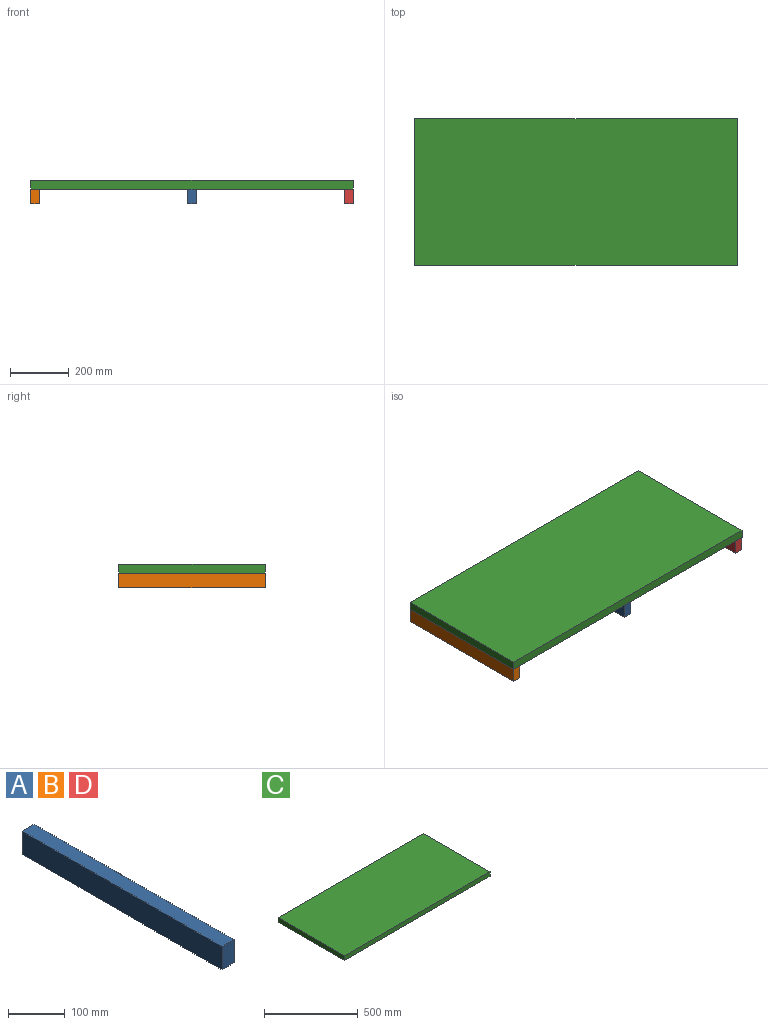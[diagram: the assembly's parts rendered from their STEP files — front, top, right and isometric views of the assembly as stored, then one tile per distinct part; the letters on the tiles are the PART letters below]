
ASSEMBLY  parts=4 mates=9
PART A: 6 faces, bbox 30x500x50 mm
  f0: plane 50x30mm, normal (0,-1,0), area 1500mm2, adj f1,f3,f4,f5
  f1: plane 500x30mm, normal (0,0,1), area 15000mm2, adj f0,f2,f4,f5
  f2: plane 50x30mm, normal (0,1,0), area 1500mm2, adj f1,f3,f4,f5
  f3: plane 500x30mm, normal (0,0,-1), area 15000mm2, adj f0,f2,f4,f5
  f4: plane 500x50mm, normal (1,0,0), area 25000mm2, adj f0,f1,f2,f3
  f5: plane 500x50mm, normal (-1,0,0), area 25000mm2, adj f0,f1,f2,f3
PART B: same geometry as A
PART C: 6 faces, bbox 1100x500x30 mm
  f0: plane 1100x30mm, normal (0,1,0), area 33000mm2, adj f1,f3,f4,f5
  f1: plane 500x30mm, normal (-1,0,0), area 15000mm2, adj f0,f2,f4,f5
  f2: plane 1100x30mm, normal (0,-1,0), area 33000mm2, adj f1,f3,f4,f5
  f3: plane 500x30mm, normal (1,0,0), area 15000mm2, adj f0,f2,f4,f5
  f4: plane 1100x500mm, normal (0,0,-1), area 550000mm2, adj f0,f1,f2,f3
  f5: plane 1100x500mm, normal (0,0,1), area 550000mm2, adj f0,f1,f2,f3
PART D: same geometry as A
PLACE A rot(axis=(1,0,0),180deg) t=(535,-640,-110)mm
PLACE B rot(axis=(1,0,0),0deg) t=(0,0,0)mm
PLACE C at identity
PLACE D rot(axis=(0.22,0.11,0.97),0deg) t=(1070,0,0)mm
MATE planar C.f2 <-> A.f2  axis (0,-1,0) through (0,-570,-30)mm
MATE planar D.f1 <-> C.f4  axis (0,0,1) through (535,-320,-30)mm
MATE planar C.f2 <-> D.f0  axis (0,-1,0) through (0,-570,-15)mm
MATE planar C.f4 <-> A.f3  axis (0,0,-1) through (0,-320,-30)mm
MATE planar C.f2 <-> A.f2  axis (0,-1,0) through (0,-570,-15)mm
MATE planar C.f4 <-> B.f1  axis (0,0,-1) through (0,-320,-30)mm
MATE planar B.f5 <-> C.f1  axis (-1,0,0) through (-550,-320,-55)mm
MATE planar B.f0 <-> C.f2  axis (0,-1,0) through (-535,-570,-55)mm
MATE planar D.f4 <-> C.f3  axis (1,0,0) through (550,-320,-55)mm
